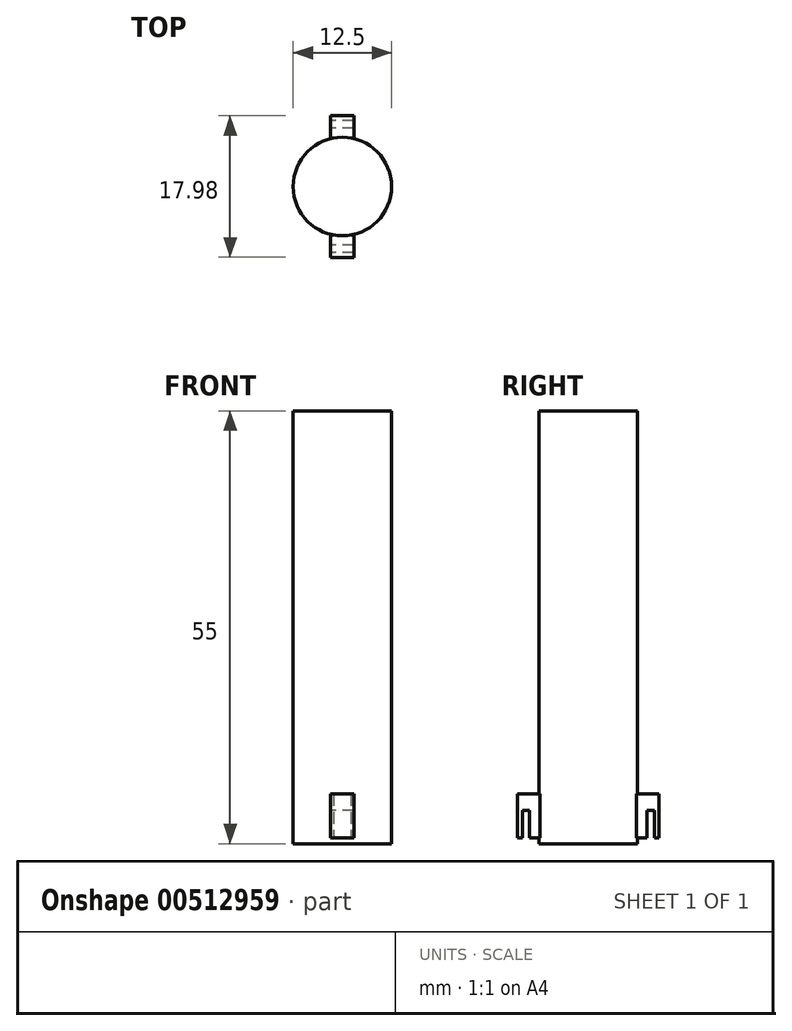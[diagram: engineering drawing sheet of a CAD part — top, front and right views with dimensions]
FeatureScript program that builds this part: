
annotation { "Feature Type Name" : "Feature", "Feature Type Description" : "" }
export const myFeature = defineFeature(function(context is Context, id is Id, definition is map)
    precondition{}
    {
        {
            var Q0;
            Q0=qCreatedBy(makeId("Top.planeOp"),FACE);
            var sketch = newSketch(context, id + "F0", { "sketchPlane" : qUnion([Q0])});
            skCircle(sketch, "E0", {"center": v(0, 0) * mm, "radius": 6.25 * mm});
            skSolve(sketch);
        }
        {
            var Q0;
            Q0=makeQuery(id+"F0.imprint","IMPRINT",FACE,{"disambiguationData":[TD([[makeQuery(id+"F0.imprint","IMPRINT",EDGE,{"derivedFrom":sQuery(id+"F0.wireOp",EDGE,"E0")}),1.0]])]});
            extrude(context, id + "F1", {"entities" : qUnion([Q0]), "depth" : 55 * mm, "offsetDistance" : 25 * mm});
        }
        {
            var Q0;
            Q0=qCreatedBy(makeId("Right.planeOp"),FACE);
            var sketch = newSketch(context, id + "F2", { "sketchPlane" : qUnion([Q0])});
            skLineSegment(sketch, "E1.bottom", {"start": v(-6.15, 6.33) * mm, "end": v(-9, 6.33) * mm});
            skLineSegment(sketch, "E1.top", {"start": v(-6.15, 0.73) * mm, "end": v(-7.45, 0.73) * mm});
            skLineSegment(sketch, "E1.left", {"start": v(-6.15, 6.33) * mm, "end": v(-6.15, 0.73) * mm});
            skLineSegment(sketch, "E1.right", {"start": v(-9, 6.33) * mm, "end": v(-9, 0.73) * mm});
            skLineSegment(sketch, "E2.left", {"start": v(-7.45, 4.24) * mm, "end": v(-7.45, 0.73) * mm});
            skLineSegment(sketch, "E2.right", {"start": v(-8.38, 4.24) * mm, "end": v(-8.38, 0.73) * mm});
            skLineSegment(sketch, "E3.trimOffspring", {"start": v(-8.38, 0.73) * mm, "end": v(-9, 0.73) * mm});
            skPoint(sketch, "E4.start.orphan", {"position": v(0, -7.13) * mm});
            skLineSegment(sketch, "E5", {"start": v(-7.45, 4.24) * mm, "end": v(-8.38, 4.24) * mm});
            skLineSegment(sketch, "E6", {"start": v(0, 61) * mm, "end": v(0, -9.16) * mm, "construction": true});
            skLineSegment(sketch, "E7.MirrorCS", {"start": v(6.15, 6.33) * mm, "end": v(6.15, 0.73) * mm});
            skLineSegment(sketch, "E8.MirrorCS", {"start": v(6.15, 6.33) * mm, "end": v(9, 6.33) * mm});
            skLineSegment(sketch, "E9.MirrorCS", {"start": v(9, 6.33) * mm, "end": v(9, 0.73) * mm});
            skLineSegment(sketch, "E10.MirrorCS", {"start": v(8.38, 0.73) * mm, "end": v(9, 0.73) * mm});
            skLineSegment(sketch, "E11.MirrorCS", {"start": v(8.38, 4.24) * mm, "end": v(8.38, 0.73) * mm});
            skLineSegment(sketch, "E12.MirrorCS", {"start": v(7.45, 4.24) * mm, "end": v(8.38, 4.24) * mm});
            skLineSegment(sketch, "E13.MirrorCS", {"start": v(7.45, 4.24) * mm, "end": v(7.45, 0.73) * mm});
            skLineSegment(sketch, "E14.MirrorCS", {"start": v(6.15, 0.73) * mm, "end": v(7.45, 0.73) * mm});
            skSolve(sketch);
        }
        {
            var Q0;
            Q0 = qSketchRegion(id + "F2", true);
            extrude(context, id + "F3", {"entities" : qUnion([Q0]), "operationType" : NewBodyOperationType.ADD, "endBound" : BoundingType.SYMMETRIC, "depth" : 3 * mm, "offsetDistance" : 25 * mm});
        }
    });
